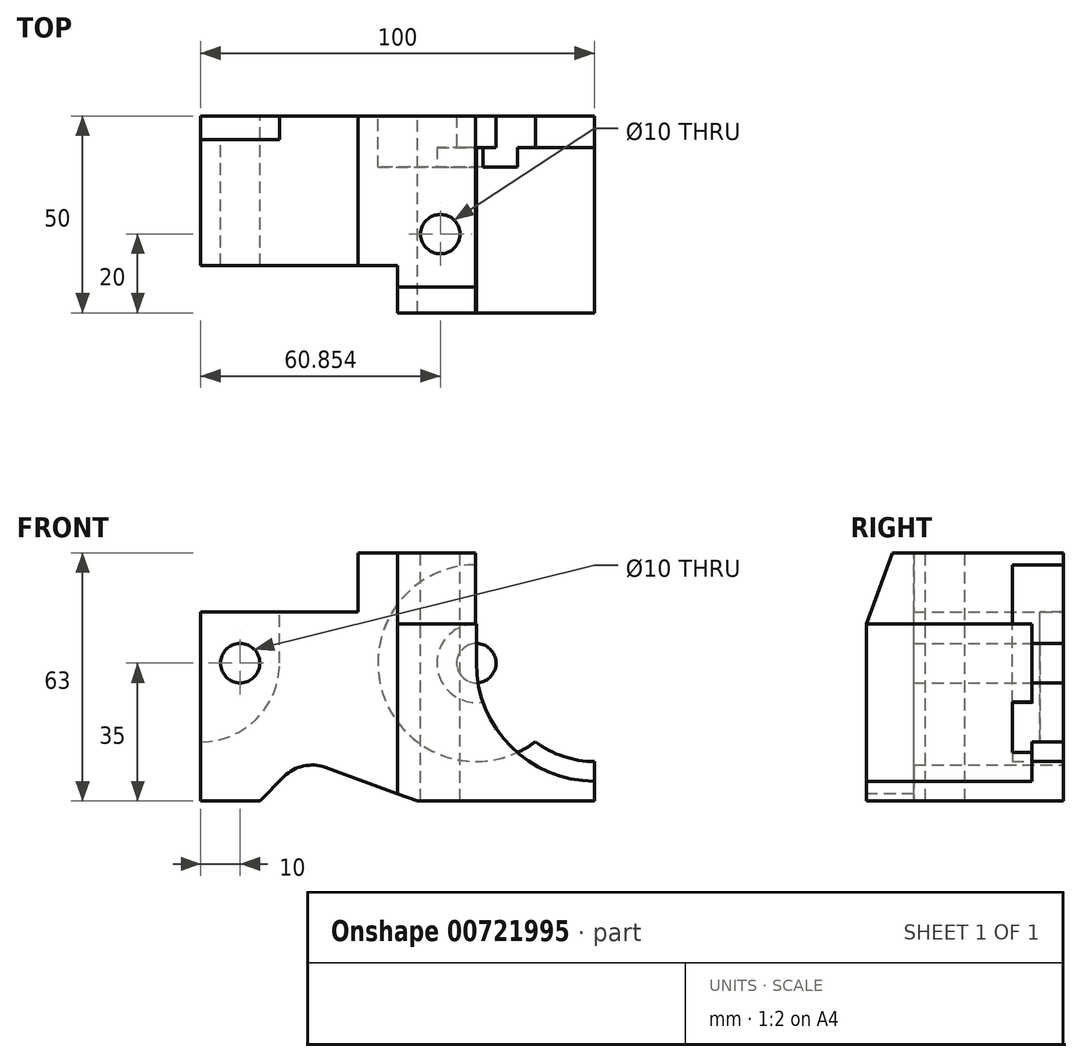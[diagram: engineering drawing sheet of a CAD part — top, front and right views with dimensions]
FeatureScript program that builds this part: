
annotation { "Feature Type Name" : "Feature", "Feature Type Description" : "" }
export const myFeature = defineFeature(function(context is Context, id is Id, definition is map)
    precondition{}
    {
        {
            var Q0;
            Q0=qCreatedBy(makeId("Right.planeOp"),FACE);
            var sketch = newSketch(context, id + "F0", { "sketchPlane" : qUnion([Q0])});
            skLineSegment(sketch, "E0.bottom", {"start": v(-25, -31.5) * mm, "end": v(25, -31.5) * mm});
            skLineSegment(sketch, "E0.top", {"start": v(-25, 31.5) * mm, "end": v(25, 31.5) * mm});
            skLineSegment(sketch, "E0.left", {"start": v(-25, -31.5) * mm, "end": v(-25, 31.5) * mm});
            skLineSegment(sketch, "E0.right", {"start": v(25, -31.5) * mm, "end": v(25, 31.5) * mm});
            skPoint(sketch, "E0.middle", {"position": v(0, 0) * mm});
            skSolve(sketch);
        }
        {
            var Q0;
            Q0=makeQuery(id+"F0.imprint","IMPRINT",FACE,{"disambiguationData":[TD([[makeQuery(id+"F0.imprint","IMPRINT",EDGE,{"derivedFrom":sQuery(id+"F0.wireOp",EDGE,"E0.bottom")}),1.0]])]});
            extrude(context, id + "F1", {"entities" : qUnion([Q0]), "depth" : 100 * mm, "offsetDistance" : 25 * mm});
        }
        {
            var Q0;
            Q0=makeQuery(id+"F1.opExtrude","CAP_FACE",FACE,{"disambiguationData":[OSD([sQuery(id+"F0.wireOp",EDGE,"E0.bottom"),sQuery(id+"F0.wireOp",EDGE,"E0.top"),sQuery(id+"F0.wireOp",EDGE,"E0.left"),sQuery(id+"F0.wireOp",EDGE,"E0.right")])],"isStart":false});
            var sketch = newSketch(context, id + "F2", { "sketchPlane" : qUnion([Q0])});
            skLineSegment(sketch, "E1", {"start": v(-25, 13.5) * mm, "end": v(-18.45, 31.5) * mm});
            skLineSegment(sketch, "E2", {"start": v(-18.45, 31.5) * mm, "end": v(-25, 31.5) * mm});
            skLineSegment(sketch, "E3", {"start": v(-25, 31.5) * mm, "end": v(-25, 13.5) * mm});
            skSolve(sketch);
        }
        {
            var Q0;
            Q0 = qSketchRegion(id + "F2", true);
            extrude(context, id + "F3", {"entities" : qUnion([Q0]), "operationType" : NewBodyOperationType.REMOVE, "endBound" : BoundingType.UP_TO_NEXT, "oppositeDirection" : true, "depth" : 25 * mm, "offsetDistance" : 25 * mm});
        }
        {
            var Q0;
            Q0=makeQuery(id+"F1.opExtrude","SWEPT_FACE",FACE,{"disambiguationData":[OSD([sQuery(id+"F0.wireOp",EDGE,"E0.left")])]});
            var sketch = newSketch(context, id + "F4", { "sketchPlane" : qUnion([Q0])});
            skArc(sketch, "E4", {"start": v(70, 3.5) * mm, "mid": v(121.21, -17.71) * mm, "end": v(100, 33.5) * mm});
            skLineSegment(sketch, "E5", {"start": v(70, 3.5) * mm, "end": v(70, 33.5) * mm});
            skLineSegment(sketch, "E6", {"start": v(70, 33.5) * mm, "end": v(100, 33.5) * mm});
            skLineSegment(sketch, "E7", {"start": v(70, 3.5) * mm, "end": v(100, 3.5) * mm, "construction": true});
            skSolve(sketch);
        }
        {
            var Q0;
            {var subQ0=sQuery(id+"F4.wireOp",EDGE,"E4");var subQ1=sQuery(id+"F0.wireOp",EDGE,"E0.left");var subQ4=makeQuery(id+"F1.opExtrude","CAP_EDGE",EDGE,{"disambiguationData":[OSD([subQ1])],"isStart":false});var subQ5=makeQuery(id+"F4.imprint","INTERSECT",VERTEX,{"derivedFrom":[subQ4,subQ0]});Q0=makeQuery(id+"F4.imprint","IMPRINT",FACE,{"disambiguationData":[TD([[makeQuery(id+"F4.imprint","IMPRINT",EDGE,{"disambiguationData":[TD([[subQ5,1.0]])],"derivedFrom":subQ0}),1.0]])]});}
            var Q1;
            {var subQ0=sQuery(id+"F4.wireOp",EDGE,"E4");var subQ1=sQuery(id+"F0.wireOp",EDGE,"E0.left");var subQ4=makeQuery(id+"F1.opExtrude","CAP_EDGE",EDGE,{"disambiguationData":[OSD([subQ1])],"isStart":false});var subQ5=makeQuery(id+"F4.imprint","INTERSECT",VERTEX,{"derivedFrom":[subQ4,subQ0]});Q1=makeQuery(id+"F4.imprint","IMPRINT",FACE,{"disambiguationData":[TD([[makeQuery(id+"F4.imprint","IMPRINT",EDGE,{"disambiguationData":[TD([[subQ5,-1.0]])],"derivedFrom":subQ0}),1.0]])]});}
            extrude(context, id + "F5", {"entities" : qUnion([Q0, Q1]), "operationType" : NewBodyOperationType.REMOVE, "oppositeDirection" : true, "depth" : 42 * mm, "offsetDistance" : 25 * mm});
        }
        {
            var Q0;
            {var subQ0=sQuery(id+"F0.wireOp",EDGE,"E0.left");var subQ1=makeQuery(id+"F1.opExtrude","CAP_EDGE",EDGE,{"disambiguationData":[OSD([subQ0])],"isStart":true});Q0=makeQuery(id+"F4.imprint","IMPRINT",FACE,{"disambiguationData":[TD([[makeQuery(id+"F4.imprint","IMPRINT",EDGE,{"derivedFrom":subQ1}),-1.0]])]});}
            var sketch = newSketch(context, id + "F6", { "sketchPlane" : qUnion([Q0])});
            skCircle(sketch, "E8", {"center": v(100, 3.5) * mm, "radius": 25 * mm});
            skSolve(sketch);
        }
        {
            var Q0;
            Q0 = qSketchRegion(id + "F6", true);
            extrude(context, id + "F7", {"entities" : qUnion([Q0]), "operationType" : NewBodyOperationType.REMOVE, "endBound" : BoundingType.THROUGH_ALL, "oppositeDirection" : true, "depth" : 25 * mm, "offsetDistance" : 25 * mm});
        }
        {
            var Q0;
            Q0=makeQuery(id+"F1.opExtrude","SWEPT_FACE",FACE,{"disambiguationData":[OSD([sQuery(id+"F0.wireOp",EDGE,"E0.right")])]});
            var sketch = newSketch(context, id + "F8", { "sketchPlane" : qUnion([Q0])});
            skCircle(sketch, "E9", {"center": v(-70, 3.5) * mm, "radius": 25 * mm});
            skSolve(sketch);
        }
        {
            var Q0;
            {var subQ0=sQuery(id+"F8.wireOp",EDGE,"E9");var subQ1=makeQuery(id+"F7.boolean.opBoolean","INTERSECT",EDGE,{"derivedFrom":[makeQuery(id+"F1.opExtrude","SWEPT_FACE",FACE,{"disambiguationData":[OSD([sQuery(id+"F0.wireOp",EDGE,"E0.right")])]}),makeQuery(id+"F7.opExtrude","SWEPT_FACE",FACE,{"disambiguationData":[OSD([sQuery(id+"F6.wireOp",EDGE,"E8")])]})]});var subQ2=makeQuery(id+"F8.imprint","INTERSECT",VERTEX,{"disambiguationData":[OD(0.0)],"derivedFrom":[subQ1,subQ0]});Q0=makeQuery(id+"F8.imprint","IMPRINT",FACE,{"disambiguationData":[TD([[makeQuery(id+"F8.imprint","IMPRINT",EDGE,{"disambiguationData":[TD([[subQ2,1.0]])],"derivedFrom":subQ0}),1.0]])]});}
            var Q1;
            {var subQ0=sQuery(id+"F8.wireOp",EDGE,"E9");var subQ1=makeQuery(id+"F7.boolean.opBoolean","INTERSECT",EDGE,{"derivedFrom":[makeQuery(id+"F1.opExtrude","SWEPT_FACE",FACE,{"disambiguationData":[OSD([sQuery(id+"F0.wireOp",EDGE,"E0.right")])]}),makeQuery(id+"F7.opExtrude","SWEPT_FACE",FACE,{"disambiguationData":[OSD([sQuery(id+"F6.wireOp",EDGE,"E8")])]})]});var subQ2=makeQuery(id+"F8.imprint","INTERSECT",VERTEX,{"disambiguationData":[OD(0.0)],"derivedFrom":[subQ1,subQ0]});Q1=makeQuery(id+"F8.imprint","IMPRINT",FACE,{"disambiguationData":[TD([[makeQuery(id+"F8.imprint","IMPRINT",EDGE,{"disambiguationData":[TD([[subQ2,-1.0]])],"derivedFrom":subQ0}),1.0]])]});}
            extrude(context, id + "F9", {"entities" : qUnion([Q0, Q1]), "operationType" : NewBodyOperationType.REMOVE, "oppositeDirection" : true, "depth" : 13 * mm, "offsetDistance" : 25 * mm});
        }
        {
            var Q0;
            {var subQ0=sQuery(id+"F0.wireOp",EDGE,"E0.left");var subQ1=makeQuery(id+"F1.opExtrude","CAP_EDGE",EDGE,{"disambiguationData":[OSD([subQ0])],"isStart":true});Q0=makeQuery(id+"F4.imprint","IMPRINT",FACE,{"disambiguationData":[TD([[makeQuery(id+"F4.imprint","IMPRINT",EDGE,{"derivedFrom":subQ1}),-1.0]])]});}
            var sketch = newSketch(context, id + "F10", { "sketchPlane" : qUnion([Q0])});
            skLineSegment(sketch, "E10.bottom", {"start": v(100, 33.69) * mm, "end": v(69.85, 33.69) * mm});
            skLineSegment(sketch, "E10.top", {"start": v(100, 3.5) * mm, "end": v(69.85, 3.5) * mm});
            skLineSegment(sketch, "E10.left", {"start": v(100, 33.69) * mm, "end": v(100, 3.5) * mm});
            skLineSegment(sketch, "E10.right", {"start": v(69.85, 33.69) * mm, "end": v(69.85, 3.5) * mm});
            skSolve(sketch);
        }
        {
            var Q0;
            {var subQ1=sQuery(id+"F10.wireOp",EDGE,"E10.bottom");Q0=makeQuery(id+"F10.imprint","IMPRINT",FACE,{"disambiguationData":[TD([[makeQuery(id+"F10.imprint","IMPRINT",EDGE,{"derivedFrom":subQ1}),1.0]])]});}
            extrude(context, id + "F11", {"entities" : qUnion([Q0]), "operationType" : NewBodyOperationType.REMOVE, "endBound" : BoundingType.THROUGH_ALL, "oppositeDirection" : true, "depth" : 25 * mm, "offsetDistance" : 25 * mm});
        }
        {
            var Q0;
            Q0=makeQuery(id+"F9.boolean.opBoolean","COPY",FACE,{"derivedFrom":makeQuery(id+"F9.opExtrude","CAP_FACE",FACE,{"disambiguationData":[OSD([sQuery(id+"F8.wireOp",EDGE,"E9")])],"isStart":false})});
            var sketch = newSketch(context, id + "F12", { "sketchPlane" : qUnion([Q0])});
            skCircle(sketch, "E11", {"center": v(-70, 3.5) * mm, "radius": 10 * mm});
            skSolve(sketch);
        }
        {
            var Q0;
            {var subQ1=makeQuery(id+"F9.opExtrude","CAP_FACE",FACE,{"disambiguationData":[OSD([sQuery(id+"F8.wireOp",EDGE,"E9")])],"isStart":false});var subQ2=makeQuery(id+"F9.boolean.opBoolean","INTERSECT",EDGE,{"derivedFrom":[makeQuery(id+"F5.boolean.opBoolean","COPY",FACE,{"derivedFrom":makeQuery(id+"F5.opExtrude","SWEPT_FACE",FACE,{"disambiguationData":[OSD([sQuery(id+"F4.wireOp",EDGE,"E5")])]})}),subQ1]});Q0=makeQuery(id+"F12.imprint","IMPRINT",FACE,{"disambiguationData":[TD([[makeQuery(id+"F12.imprint","IMPRINT",EDGE,{"derivedFrom":subQ2}),-1.0]])]});}
            extrude(context, id + "F13", {"entities" : qUnion([Q0]), "operationType" : NewBodyOperationType.ADD, "depth" : (13 - 8) * mm, "offsetDistance" : 25 * mm});
        }
        {
            var Q0;
            Q0=makeQuery(id+"F13.opExtrude","CAP_FACE",FACE,{"disambiguationData":[OSD([sQuery(id+"F4.wireOp",EDGE,"E4"),sQuery(id+"F4.wireOp",EDGE,"E5"),sQuery(id+"F8.wireOp",EDGE,"E9"),sQuery(id+"F12.wireOp",EDGE,"E11")])],"isStart":false});
            var sketch = newSketch(context, id + "F14", { "sketchPlane" : qUnion([Q0])});
            skCircle(sketch, "E12", {"center": v(-70, 3.5) * mm, "radius": 5 * mm});
            skSolve(sketch);
        }
        {
            var Q0;
            {var subQ0=sQuery(id+"F14.wireOp",EDGE,"E12");var subQ1=sQuery(id+"F8.wireOp",EDGE,"E9");var subQ2=makeQuery(id+"F13.opExtrude","CAP_EDGE",EDGE,{"disambiguationData":[OSD([sQuery(id+"F4.wireOp",EDGE,"E5"),subQ1])],"isStart":false});var subQ3=makeQuery(id+"F14.imprint","INTERSECT",VERTEX,{"derivedFrom":[subQ2,subQ0]});Q0=makeQuery(id+"F14.imprint","IMPRINT",FACE,{"disambiguationData":[TD([[makeQuery(id+"F14.imprint","IMPRINT",EDGE,{"disambiguationData":[TD([[subQ3,-1.0]])],"derivedFrom":subQ0}),1.0]])]});}
            var Q1;
            {var subQ0=sQuery(id+"F14.wireOp",EDGE,"E12");var subQ1=sQuery(id+"F8.wireOp",EDGE,"E9");var subQ2=makeQuery(id+"F13.opExtrude","CAP_EDGE",EDGE,{"disambiguationData":[OSD([sQuery(id+"F4.wireOp",EDGE,"E5"),subQ1])],"isStart":false});var subQ3=makeQuery(id+"F14.imprint","INTERSECT",VERTEX,{"derivedFrom":[subQ2,subQ0]});Q1=makeQuery(id+"F14.imprint","IMPRINT",FACE,{"disambiguationData":[TD([[makeQuery(id+"F14.imprint","IMPRINT",EDGE,{"disambiguationData":[TD([[subQ3,1.0]])],"derivedFrom":subQ0}),1.0]])]});}
            var Q2;
            Q2=makeQuery(id+"F1.opExtrude","SWEPT_FACE",FACE,{"disambiguationData":[OSD([sQuery(id+"F0.wireOp",EDGE,"E0.right")])]});
            extrude(context, id + "F15", {"entities" : qUnion([Q0, Q1]), "operationType" : NewBodyOperationType.ADD, "endBound" : BoundingType.UP_TO_SURFACE, "depth" : 25 * mm, "endBoundEntityFace" : qUnion([Q2]), "offsetDistance" : 25 * mm});
        }
        {
            var Q0;
            Q0=makeQuery(id+"F1.opExtrude","SWEPT_FACE",FACE,{"disambiguationData":[OSD([sQuery(id+"F0.wireOp",EDGE,"E0.right")])]});
            var sketch = newSketch(context, id + "F16", { "sketchPlane" : qUnion([Q0])});
            skLineSegment(sketch, "E13.bottom", {"start": v(0, 31.5) * mm, "end": v(-40, 31.5) * mm});
            skLineSegment(sketch, "E13.top", {"start": v(0, 16.5) * mm, "end": v(-40, 16.5) * mm});
            skLineSegment(sketch, "E13.left", {"start": v(0, 31.5) * mm, "end": v(0, 16.5) * mm});
            skLineSegment(sketch, "E13.right", {"start": v(-40, 31.5) * mm, "end": v(-40, 16.5) * mm});
            skSolve(sketch);
        }
        {
            var Q0;
            Q0=makeQuery(id+"F16.imprint","IMPRINT",FACE,{"disambiguationData":[TD([[makeQuery(id+"F16.imprint","IMPRINT",EDGE,{"derivedFrom":sQuery(id+"F16.wireOp",EDGE,"E13.bottom")}),-1.0]])]});
            extrude(context, id + "F17", {"entities" : qUnion([Q0]), "operationType" : NewBodyOperationType.REMOVE, "endBound" : BoundingType.UP_TO_NEXT, "oppositeDirection" : true, "depth" : 25 * mm, "offsetDistance" : 25 * mm});
        }
        {
            var Q0;
            Q0=makeQuery(id+"F1.opExtrude","SWEPT_FACE",FACE,{"disambiguationData":[OSD([sQuery(id+"F0.wireOp",EDGE,"E0.right")])]});
            var sketch = newSketch(context, id + "F18", { "sketchPlane" : qUnion([Q0])});
            skArc(sketch, "E14", {"start": v(-20, 3.5) * mm, "mid": v(14.14, -10.64) * mm, "end": v(0, 23.5) * mm});
            skLineSegment(sketch, "E15", {"start": v(-20, 3.5) * mm, "end": v(-20, 23.5) * mm});
            skLineSegment(sketch, "E16", {"start": v(-20, 23.5) * mm, "end": v(0, 23.5) * mm});
            skLineSegment(sketch, "E17", {"start": v(-20, 3.5) * mm, "end": v(0, 3.5) * mm, "construction": true});
            skSolve(sketch);
        }
        {
            var Q0;
            {var subQ0=sQuery(id+"F18.wireOp",EDGE,"E16");Q0=makeQuery(id+"F18.imprint","IMPRINT",FACE,{"disambiguationData":[TD([[makeQuery(id+"F18.imprint","IMPRINT",EDGE,{"derivedFrom":subQ0}),-1.0]])]});}
            var Q1;
            {var subQ0=sQuery(id+"F18.wireOp",EDGE,"E15");var subQ1=sQuery(id+"F18.wireOp",EDGE,"E14");var subQ2=makeQuery(id+"F18.imprint","INTERSECT",VERTEX,{"derivedFrom":[subQ1,subQ0]});Q1=makeQuery(id+"F18.imprint","IMPRINT",FACE,{"disambiguationData":[TD([[makeQuery(id+"F18.imprint","IMPRINT",EDGE,{"disambiguationData":[TD([[subQ2,-1.0]])],"derivedFrom":subQ1}),1.0]])]});}
            extrude(context, id + "F19", {"entities" : qUnion([Q0, Q1]), "operationType" : NewBodyOperationType.REMOVE, "oppositeDirection" : true, "depth" : 6 * mm, "offsetDistance" : 25 * mm});
        }
        {
            var Q0;
            Q0=makeQuery(id+"F19.boolean.opBoolean","COPY",FACE,{"derivedFrom":makeQuery(id+"F19.opExtrude","CAP_FACE",FACE,{"disambiguationData":[OSD([sQuery(id+"F18.wireOp",EDGE,"E14"),sQuery(id+"F18.wireOp",EDGE,"E15"),sQuery(id+"F18.wireOp",EDGE,"E16")])],"isStart":false})});
            var sketch = newSketch(context, id + "F20", { "sketchPlane" : qUnion([Q0])});
            skCircle(sketch, "E18", {"center": v(-10, 3.5) * mm, "radius": 5 * mm});
            skSolve(sketch);
        }
        {
            var Q0;
            Q0 = qSketchRegion(id + "F20", true);
            extrude(context, id + "F21", {"entities" : qUnion([Q0]), "operationType" : NewBodyOperationType.REMOVE, "endBound" : BoundingType.THROUGH_ALL, "oppositeDirection" : true, "depth" : 25 * mm, "offsetDistance" : 25 * mm});
        }
        {
            var Q0;
            Q0=makeQuery(id+"F1.opExtrude","SWEPT_FACE",FACE,{"disambiguationData":[OSD([sQuery(id+"F0.wireOp",EDGE,"E0.right")])]});
            var sketch = newSketch(context, id + "F22", { "sketchPlane" : qUnion([Q0])});
            skLineSegment(sketch, "E19", {"start": v(-55, -31.5) * mm, "end": v(-31.66, -23) * mm});
            skLineSegment(sketch, "E20", {"start": v(-21.17, -25.33) * mm, "end": v(-15, -31.5) * mm});
            skArc(sketch, "E21", {"start": v(-21.17, -25.33) * mm, "mid": v(-26.08, -22.64) * mm, "end": v(-31.66, -23) * mm});
            skSolve(sketch);
        }
        {
            var Q0;
            {var subQ0=sQuery(id+"F22.wireOp",EDGE,"E19");Q0=makeQuery(id+"F22.imprint","IMPRINT",FACE,{"disambiguationData":[TD([[makeQuery(id+"F22.imprint","IMPRINT",EDGE,{"derivedFrom":subQ0}),-1.0]])]});}
            extrude(context, id + "F23", {"entities" : qUnion([Q0]), "operationType" : NewBodyOperationType.REMOVE, "endBound" : BoundingType.THROUGH_ALL, "oppositeDirection" : true, "depth" : 25 * mm, "offsetDistance" : 25 * mm});
        }
        {
            var Q0;
            Q0=makeQuery(id+"F1.opExtrude","SWEPT_FACE",FACE,{"disambiguationData":[OSD([sQuery(id+"F0.wireOp",EDGE,"E0.top")])]});
            var sketch = newSketch(context, id + "F24", { "sketchPlane" : qUnion([Q0])});
            skLineSegment(sketch, "E22.bottom", {"start": v(0, -25) * mm, "end": v(50, -25) * mm});
            skLineSegment(sketch, "E22.top", {"start": v(0, -13) * mm, "end": v(50, -13) * mm});
            skLineSegment(sketch, "E22.left", {"start": v(0, -25) * mm, "end": v(0, -13) * mm});
            skLineSegment(sketch, "E22.right", {"start": v(50, -25) * mm, "end": v(50, -13) * mm});
            skSolve(sketch);
        }
        {
            var Q0;
            Q0 = qSketchRegion(id + "F24", true);
            extrude(context, id + "F25", {"entities" : qUnion([Q0]), "operationType" : NewBodyOperationType.REMOVE, "endBound" : BoundingType.THROUGH_ALL, "oppositeDirection" : true, "depth" : 25 * mm, "offsetDistance" : 25 * mm});
        }
        {
            var Q0;
            Q0=makeQuery(id+"F1.opExtrude","SWEPT_FACE",FACE,{"disambiguationData":[OSD([sQuery(id+"F0.wireOp",EDGE,"E0.top")])]});
            var sketch = newSketch(context, id + "F26", { "sketchPlane" : qUnion([Q0])});
            skCircle(sketch, "E23", {"center": v(60.85, -5) * mm, "radius": 5 * mm});
            skSolve(sketch);
        }
        {
            var Q0;
            Q0=makeQuery(id+"F26.imprint","IMPRINT",FACE,{"disambiguationData":[TD([[makeQuery(id+"F26.imprint","IMPRINT",EDGE,{"derivedFrom":sQuery(id+"F26.wireOp",EDGE,"E23")}),1.0]])]});
            extrude(context, id + "F27", {"entities" : qUnion([Q0]), "operationType" : NewBodyOperationType.REMOVE, "endBound" : BoundingType.THROUGH_ALL, "oppositeDirection" : true, "depth" : 25 * mm, "offsetDistance" : 25 * mm});
        }
    });
